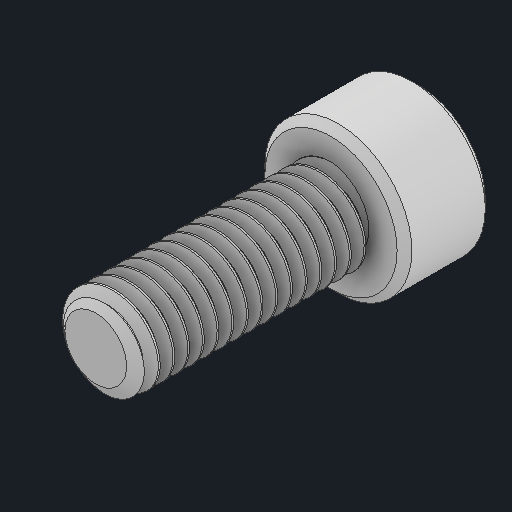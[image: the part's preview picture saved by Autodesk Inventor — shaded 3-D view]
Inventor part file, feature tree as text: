
AUTODESK INVENTOR PART (.ipt)
format: ipt  version: 2024 (Build 280153000, 153)  size: 679,424 bytes
history: native  units: in
note: dims shown in document units (in); Inventor stores cm internally (conversion verified against a paired STEP export)
features: chamfer x1
ambient origin geometry x8: Origin, YZ Plane, XZ Plane, XY Plane, X Axis, Y Axis, Z Axis, Center Point
bodies: Solid1 (feature_tree)
feature tree (1):
  chamfer  "Chamfer1"  [1 undecoded]
note: 1 required parameter value undecoded (feature->parameter linkage not recoverable at this tier; creation-order binding heuristic only, values carry confidence <= 0.55)
